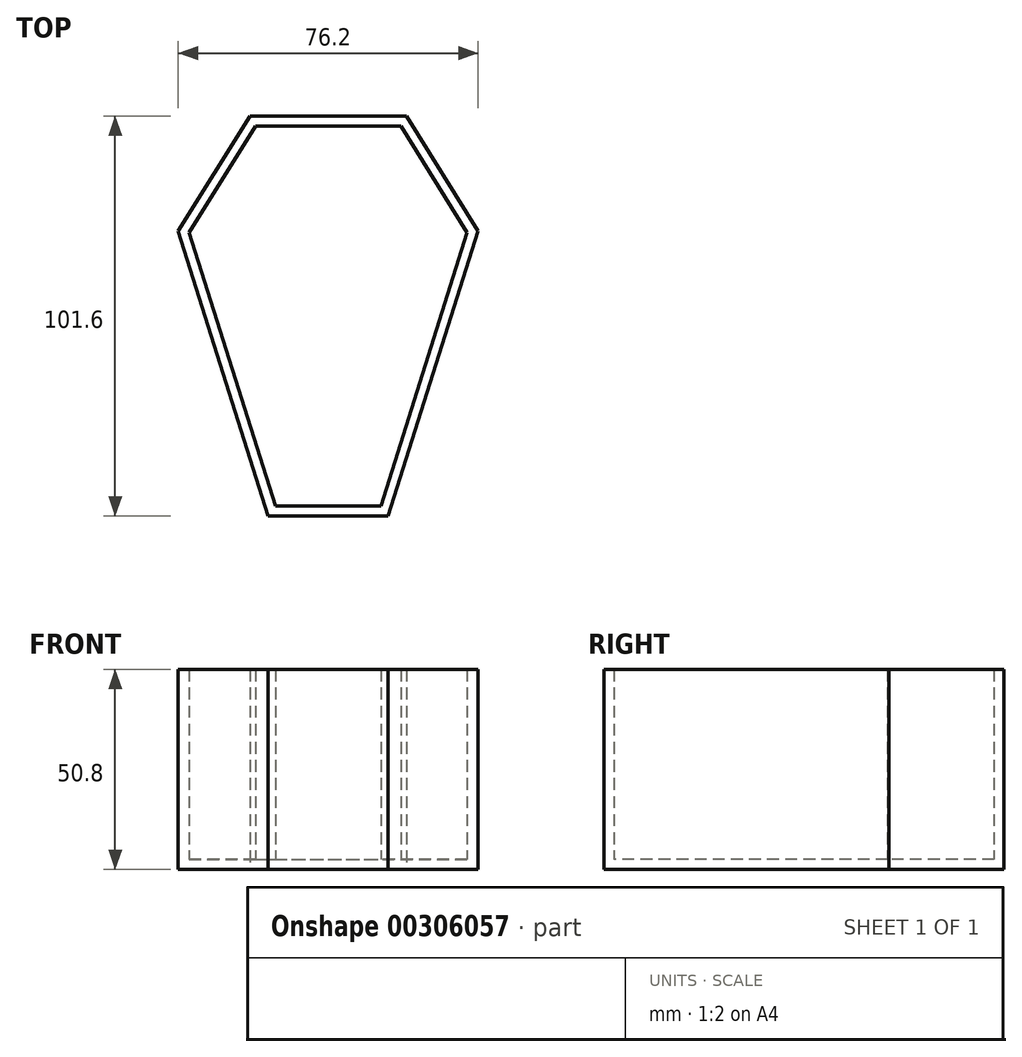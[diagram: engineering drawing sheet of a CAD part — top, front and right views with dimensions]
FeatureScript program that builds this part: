
annotation { "Feature Type Name" : "Feature", "Feature Type Description" : "" }
export const myFeature = defineFeature(function(context is Context, id is Id, definition is map)
    precondition{}
    {
        {
            var Q0;
            Q0=qCreatedBy(makeId("Top.planeOp"),FACE);
            var sketch = newSketch(context, id + "F0", { "sketchPlane" : qUnion([Q0])});
            skLineSegment(sketch, "E0.bottom", {"start": v(-38.1, 50.8) * mm, "end": v(38.1, 50.8) * mm});
            skLineSegment(sketch, "E0.top", {"start": v(-38.1, -50.8) * mm, "end": v(38.1, -50.8) * mm});
            skLineSegment(sketch, "E0.left", {"start": v(-38.1, 50.8) * mm, "end": v(-38.1, -50.8) * mm});
            skLineSegment(sketch, "E0.right", {"start": v(38.1, 50.8) * mm, "end": v(38.1, -50.8) * mm});
            skPoint(sketch, "E0.middle", {"position": v(0, 0) * mm});
            skLineSegment(sketch, "E1", {"start": v(-19.86, 50.8) * mm, "end": v(-38.1, 21.59) * mm});
            skLineSegment(sketch, "E2", {"start": v(-38.1, 21.59) * mm, "end": v(-15.25, -50.8) * mm});
            skLineSegment(sketch, "E3.MirrorCS", {"start": v(19.86, 50.8) * mm, "end": v(38.1, 21.59) * mm});
            skLineSegment(sketch, "E4.MirrorCS", {"start": v(38.1, 21.59) * mm, "end": v(15.25, -50.8) * mm});
            skSolve(sketch);
        }
        {
            var Q0;
            {var subQ0=sQuery(id+"F0.wireOp",EDGE,"E1");Q0=makeQuery(id+"F0.imprint","IMPRINT",FACE,{"disambiguationData":[TD([[makeQuery(id+"F0.imprint","IMPRINT",EDGE,{"derivedFrom":subQ0}),1.0]])]});}
            extrude(context, id + "F1", {"entities" : qUnion([Q0]), "depth" : 50.8 * mm});
        }
        {
            var Q0;
            Q0=makeQuery(id+"F1.opExtrude","CAP_FACE",FACE,{"disambiguationData":[OSD([sQuery(id+"F0.wireOp",EDGE,"E0.bottom"),sQuery(id+"F0.wireOp",EDGE,"E0.top"),sQuery(id+"F0.wireOp",EDGE,"E1"),sQuery(id+"F0.wireOp",EDGE,"E2"),sQuery(id+"F0.wireOp",EDGE,"E3.MirrorCS"),sQuery(id+"F0.wireOp",EDGE,"E4.MirrorCS")])],"isStart":false});
            shell(context, id + "F2", {"entities" : qUnion([Q0]), "thickness" : 2.54 * mm});
        }
    });
